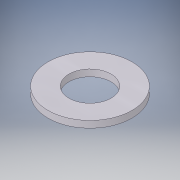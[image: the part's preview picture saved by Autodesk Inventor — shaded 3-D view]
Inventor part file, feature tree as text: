
AUTODESK INVENTOR PART (.ipt)
format: ipt  version: 2017 (Build 210142000, 142)  size: 100,864 bytes
history: native  units: in
note: dims shown in document units (in); Inventor stores cm internally (conversion verified against a paired STEP export)
features: extrude x1, hole x1, sketch x1
ambient origin geometry x8: Origin, YZ Plane, XZ Plane, XY Plane, X Axis, Y Axis, Z Axis, Center Point
bodies: Solid1 (feature_tree)
feature tree (3):
  extrude  "Extrusion1"  Depth=0.01in TaperAngle=0.0deg
  hole  "Hole1"  [1 undecoded]
  sketch  "Sketch1"  dims[d0=0.125in d1=0.01in d2=0.0in d3=1.0in d4=1.0in d5=0.0625in d6=0.75in d7=0.375in d8=0.25in d9=0.5635in d10=0.0625in d11=0.8108in]
note: 1 required parameter value undecoded (feature->parameter linkage not recoverable at this tier; creation-order binding heuristic only, values carry confidence <= 0.55)
